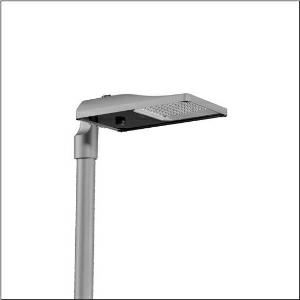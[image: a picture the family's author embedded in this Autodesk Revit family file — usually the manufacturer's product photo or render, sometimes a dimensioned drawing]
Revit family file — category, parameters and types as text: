
# Revit family: streetlight_sl_31_midi___st0_5a_5xh7b31t08na_48dc
name_source: partatom
category: Lighting Fixtures
units: mm (PartAtom-declared; Revit-internal decimal feet)

## family parameters
Cut with Voids When Loaded = No
Host = Face
Light Source = No
Part Type = Normal
Room Calculation Point = No
Round Connector Dimension = Use Diameter
Shared = No

## types (1)
- --- (1 x LED, 22750 lm, 149.5 W, 3000K)
    Apparent Load = 149 VA
    CIE Flux Codes = 43 76 97 100 100
    Color Rendering = 70
    Color Temperature = 3000K
    Default Elevation = 1800 mm
    Description = Streetlight SL 31 midi D4i, Desk-Remote mast luminaire for post-top, side-entry; light control with lens of PMMA; light distribution: ST0.5a, direct asymmetric distribution, for standard-compliant lighting for roads and squares; LED: luminous flux: 22.750lm, light colour: 730, colour temperature: 3000K; luminous efficacy: 152,2lm/W; control: pre-setting: logarithmic dimming characteristic, flexible luminous flux parameterisation, time-dependent luminous flux control, constant luminous flux control, power reduction, intelligent temperature release in ECG and LED module, overheat protection; luminaire housing, of diecast aluminium, Siteco® metallic grey (DB 702S), corrosivity category C5 high according to DIN EN ISO 12944; cover of toughened safety glass, transparent, opened without tools; mast flange of diecast aluminium, Siteco® metallic grey (DB 702S), spigot size: 76/60mm, mast flange included unmounted; with cable H07RN-F 2x 1.5mm², cable length: 12,5m, connection cable pre-assembled; mains connection: 220..240V, AC, 50/60Hz; power consumption (at start of service life): 149,5W / (at end of service life): 163,6W / (with reduced operation 50%): 66,6W; protection rating (complete): IP66; insulation class (complete): insulation class II (safety insulation); impact resistance: IK09; certification: CE, ENEC, ENEC+, VDE, UKCA, ZD4i; permissible operating ambient temperature for outdoor applications: -40..+50°C; packaging unit: 1 piece

Light Distribution: ST0.5a
    Height = 79 mm
    Lamp = 1 x LED
    Lamp Light Flux = 22750 lm
    Lamp Power = 149.5 W
    Lamp count = 1
    Length = 577 mm
    Luminous efficacy = 152 lm/W
    Manufacturer = Siteco
    ModVariant = No
    Model = 5XH7B31T08NA
    Number of Poles = 1
    OnlyDefault = Yes
    Power Factor = 1
    Product Name = Streetlight SL 31 midi | ST0.5a
    Product group = mast luminaire | pylon top
    ProductGroupID = 6100
    Protection Class = Protection class II
    Protection Degree = IP 66
    RLX_Detail_Level = 1
    RLX_Emergency_Light_Flux = 0 lm
    RLX_Emergency_Type = 0
    RLX_Emergency_Type_DB = No
    RlxData = <blob elided: 54081 chars, md5=5a54372d>
    Socket = socket
    Standby Power = 0 W
    System Light Flux = 22749 lm
    System Power = 149 W
    Type Comments = factory setting: luminous flux: 100 % | dim-lin: 254 | 795 mA
    Type Image = l_1300321.jpg
    URL = http://relux.com
    VarID = @adj_077799
    Voltage = 0 V
    Weight = 0.00 kg
    Width = 362 mm

## geometry (parser evidence)
native form markers: Blend x4, Sweep x9
no freeform markers — native parametric forms only
